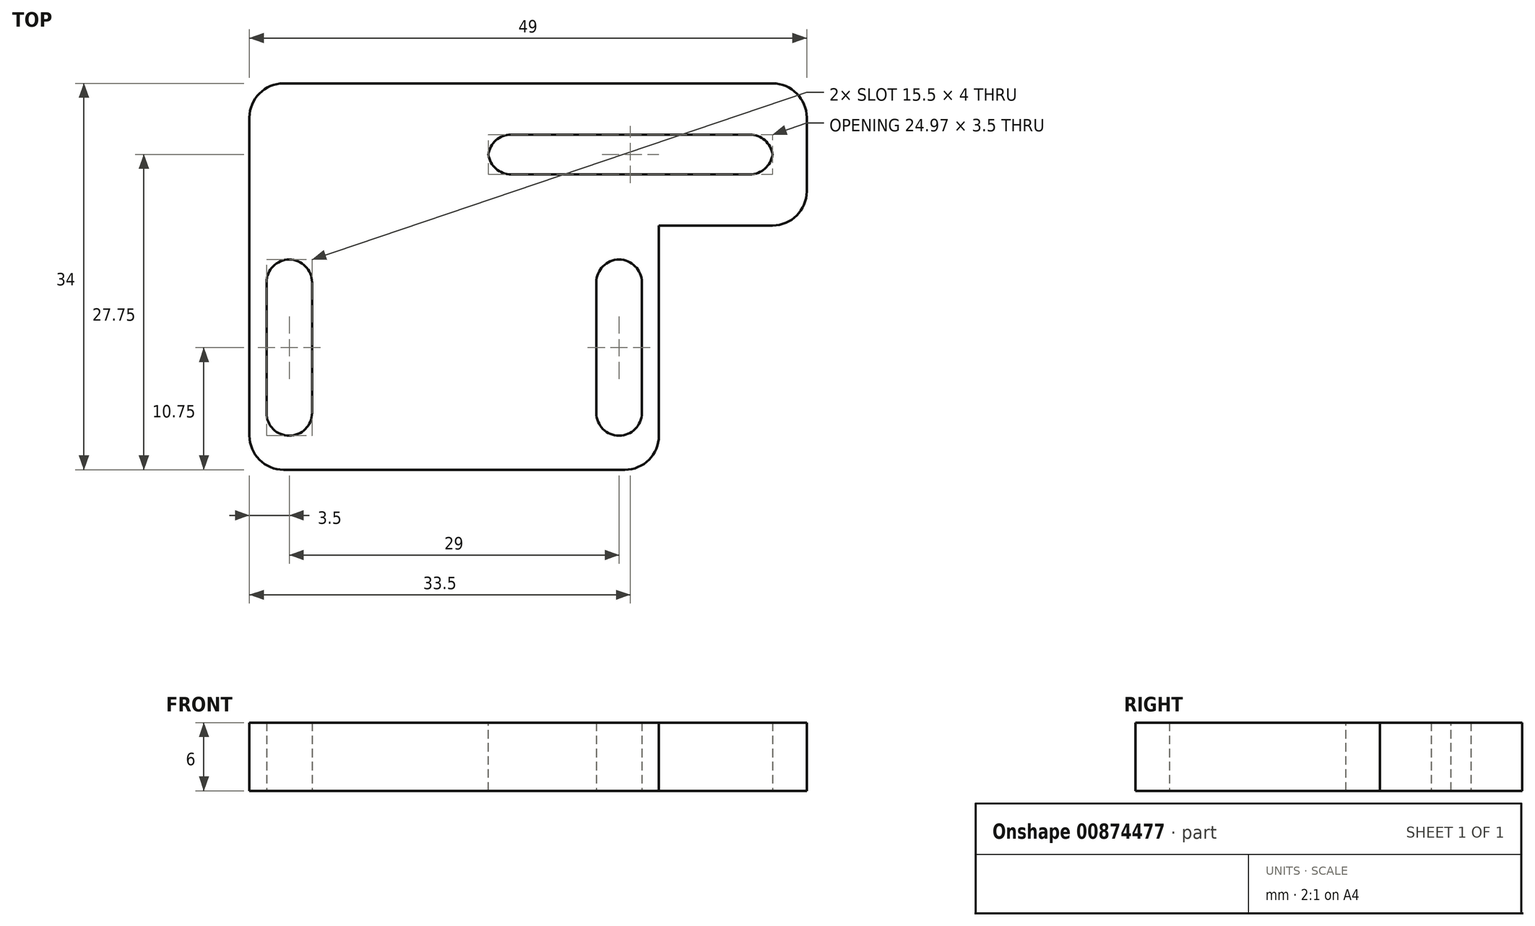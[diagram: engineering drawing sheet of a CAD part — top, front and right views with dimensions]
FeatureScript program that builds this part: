
annotation { "Feature Type Name" : "Feature", "Feature Type Description" : "" }
export const myFeature = defineFeature(function(context is Context, id is Id, definition is map)
    precondition{}
    {
        {
            var Q0;
            Q0=qCreatedBy(makeId("Top.planeOp"),FACE);
            var sketch = newSketch(context, id + "F0", { "sketchPlane" : qUnion([Q0])});
            skLineSegment(sketch, "E0.bottom", {"start": v(18, 10.75) * mm, "end": v(-18, 10.75) * mm});
            skLineSegment(sketch, "E0.top", {"start": v(18, -10.75) * mm, "end": v(-18, -10.75) * mm});
            skLineSegment(sketch, "E0.left", {"start": v(18, 10.75) * mm, "end": v(18, -10.75) * mm});
            skLineSegment(sketch, "E0.right", {"start": v(-18, 10.75) * mm, "end": v(-18, -10.75) * mm});
            skPoint(sketch, "E0.middle", {"position": v(0, 0) * mm});
            skLineSegment(sketch, "E1.bottom", {"start": v(12.5, -7.75) * mm, "end": v(16.5, -7.75) * mm});
            skLineSegment(sketch, "E1.top", {"start": v(12.5, 7.75) * mm, "end": v(16.5, 7.75) * mm});
            skLineSegment(sketch, "E1.left", {"start": v(12.5, -7.75) * mm, "end": v(12.5, 7.75) * mm});
            skLineSegment(sketch, "E1.right", {"start": v(16.5, -7.75) * mm, "end": v(16.5, 7.75) * mm});
            skPoint(sketch, "E1.middle", {"position": v(14.5, 0) * mm});
            skLineSegment(sketch, "E2.bottom", {"start": v(-12.5, 7.75) * mm, "end": v(-16.5, 7.75) * mm});
            skLineSegment(sketch, "E2.top", {"start": v(-12.5, -7.75) * mm, "end": v(-16.5, -7.75) * mm});
            skLineSegment(sketch, "E2.left", {"start": v(-12.5, 7.75) * mm, "end": v(-12.5, -7.75) * mm});
            skLineSegment(sketch, "E2.right", {"start": v(-16.5, 7.75) * mm, "end": v(-16.5, -7.75) * mm});
            skPoint(sketch, "E2.middle", {"position": v(-14.5, 0) * mm});
            skCircle(sketch, "E3", {"center": v(-4.03, -6.69) * mm, "radius": 1.63 * mm});
            skCircle(sketch, "E4", {"center": v(4.03, -6.69) * mm, "radius": 1.63 * mm});
            skLineSegment(sketch, "E5", {"start": v(-4.03, -6.69) * mm, "end": v(4.03, -6.69) * mm, "construction": true});
            skLineSegment(sketch, "E6", {"start": v(0, -6.69) * mm, "end": v(0, 0) * mm, "construction": true});
            skLineSegment(sketch, "E7.bottom", {"start": v(-18, 10.75) * mm, "end": v(31, 10.75) * mm});
            skLineSegment(sketch, "E7.top", {"start": v(-18, 23.25) * mm, "end": v(31, 23.25) * mm});
            skLineSegment(sketch, "E7.left", {"start": v(-18, 10.75) * mm, "end": v(-18, 23.25) * mm});
            skLineSegment(sketch, "E7.right", {"start": v(31, 10.75) * mm, "end": v(31, 23.25) * mm});
            skLineSegment(sketch, "E8.bottom", {"start": v(28, 18.75) * mm, "end": v(3, 18.75) * mm});
            skLineSegment(sketch, "E8.top", {"start": v(28, 15.25) * mm, "end": v(3, 15.25) * mm});
            skLineSegment(sketch, "E8.left", {"start": v(28, 18.75) * mm, "end": v(28, 15.25) * mm});
            skLineSegment(sketch, "E8.right", {"start": v(3, 18.75) * mm, "end": v(3, 15.25) * mm});
            skLineSegment(sketch, "E9", {"start": v(0, 10.75) * mm, "end": v(0, 23.25) * mm, "construction": true});
            skLineSegment(sketch, "E10", {"start": v(28, 17) * mm, "end": v(31, 17) * mm, "construction": true});
            skSolve(sketch);
        }
        {
            var Q0;
            Q0=makeQuery(id+"F0.imprint","IMPRINT",FACE,{"disambiguationData":[TD([[makeQuery(id+"F0.imprint","IMPRINT",EDGE,{"derivedFrom":sQuery(id+"F0.wireOp",EDGE,"E0.top")}),-1.0]])]});
            var Q1;
            Q1=makeQuery(id+"F0.imprint","IMPRINT",FACE,{"disambiguationData":[TD([[makeQuery(id+"F0.imprint","IMPRINT",EDGE,{"derivedFrom":sQuery(id+"F0.wireOp",EDGE,"E7.top")}),-1.0]])]});
            var Q2;
            Q2=makeQuery(id+"F0.imprint","IMPRINT",FACE,{"disambiguationData":[TD([[makeQuery(id+"F0.imprint","IMPRINT",EDGE,{"derivedFrom":sQuery(id+"F0.wireOp",EDGE,"E3")}),1.0]])]});
            var Q3;
            Q3=makeQuery(id+"F0.imprint","IMPRINT",FACE,{"disambiguationData":[TD([[makeQuery(id+"F0.imprint","IMPRINT",EDGE,{"derivedFrom":sQuery(id+"F0.wireOp",EDGE,"E4")}),1.0]])]});
            extrude(context, id + "F1", {"entities" : qUnion([Q0, Q1, Q2, Q3]), "depth" : 6 * mm, "offsetDistance" : 25 * mm});
        }
        {
            var Q0;
            Q0=makeQuery(id+"F1.opExtrude","SWEPT_EDGE",EDGE,{"disambiguationData":[OSD([sQuery(id+"F0.wireOp",EDGE,"E8.bottom"),sQuery(id+"F0.wireOp",EDGE,"E8.right")])]});
            var Q1;
            Q1=makeQuery(id+"F1.opExtrude","SWEPT_EDGE",EDGE,{"disambiguationData":[OSD([sQuery(id+"F0.wireOp",EDGE,"E8.bottom"),sQuery(id+"F0.wireOp",EDGE,"E8.left")])]});
            var Q2;
            Q2=makeQuery(id+"F1.opExtrude","SWEPT_EDGE",EDGE,{"disambiguationData":[OSD([sQuery(id+"F0.wireOp",EDGE,"E8.top"),sQuery(id+"F0.wireOp",EDGE,"E8.left")])]});
            var Q3;
            Q3=makeQuery(id+"F1.opExtrude","SWEPT_EDGE",EDGE,{"disambiguationData":[OSD([sQuery(id+"F0.wireOp",EDGE,"E8.top"),sQuery(id+"F0.wireOp",EDGE,"E8.right")])]});
            var Q4;
            Q4=makeQuery(id+"F1.opExtrude","SWEPT_EDGE",EDGE,{"disambiguationData":[OSD([sQuery(id+"F0.wireOp",EDGE,"E2.top"),sQuery(id+"F0.wireOp",EDGE,"E2.right")])]});
            var Q5;
            Q5=makeQuery(id+"F1.opExtrude","SWEPT_EDGE",EDGE,{"disambiguationData":[OSD([sQuery(id+"F0.wireOp",EDGE,"E1.bottom"),sQuery(id+"F0.wireOp",EDGE,"E1.left")])]});
            var Q6;
            Q6=makeQuery(id+"F1.opExtrude","SWEPT_EDGE",EDGE,{"disambiguationData":[OSD([sQuery(id+"F0.wireOp",EDGE,"E1.bottom"),sQuery(id+"F0.wireOp",EDGE,"E1.right")])]});
            var Q7;
            Q7=makeQuery(id+"F1.opExtrude","SWEPT_EDGE",EDGE,{"disambiguationData":[OSD([sQuery(id+"F0.wireOp",EDGE,"E2.top"),sQuery(id+"F0.wireOp",EDGE,"E2.left")])]});
            var Q8;
            Q8=makeQuery(id+"F1.opExtrude","SWEPT_EDGE",EDGE,{"disambiguationData":[OSD([sQuery(id+"F0.wireOp",EDGE,"E2.bottom"),sQuery(id+"F0.wireOp",EDGE,"E2.left")])]});
            var Q9;
            Q9=makeQuery(id+"F1.opExtrude","SWEPT_EDGE",EDGE,{"disambiguationData":[OSD([sQuery(id+"F0.wireOp",EDGE,"E2.bottom"),sQuery(id+"F0.wireOp",EDGE,"E2.right")])]});
            var Q10;
            Q10=makeQuery(id+"F1.opExtrude","SWEPT_EDGE",EDGE,{"disambiguationData":[OSD([sQuery(id+"F0.wireOp",EDGE,"E1.top"),sQuery(id+"F0.wireOp",EDGE,"E1.left")])]});
            var Q11;
            Q11=makeQuery(id+"F1.opExtrude","SWEPT_EDGE",EDGE,{"disambiguationData":[OSD([sQuery(id+"F0.wireOp",EDGE,"E1.top"),sQuery(id+"F0.wireOp",EDGE,"E1.right")])]});
            fillet(context, id + "F2", {"entities" : qUnion([Q0, Q1, Q2, Q3, Q4, Q5, Q6, Q7, Q8, Q9, Q10, Q11]), "radius" : 2 * mm, "tangentPropagation" : true, "allowEdgeOverflow" : false});
        }
        {
            var Q0;
            Q0=makeQuery(id+"F1.opExtrude","SWEPT_EDGE",EDGE,{"disambiguationData":[OSD([sQuery(id+"F0.wireOp",EDGE,"E7.bottom"),sQuery(id+"F0.wireOp",EDGE,"E7.right")])]});
            var Q1;
            Q1=makeQuery(id+"F1.opExtrude","SWEPT_EDGE",EDGE,{"disambiguationData":[OSD([sQuery(id+"F0.wireOp",EDGE,"E7.top"),sQuery(id+"F0.wireOp",EDGE,"E7.right")])]});
            var Q2;
            Q2=makeQuery(id+"F1.opExtrude","SWEPT_EDGE",EDGE,{"disambiguationData":[OSD([sQuery(id+"F0.wireOp",EDGE,"E7.top"),sQuery(id+"F0.wireOp",EDGE,"E7.left")])]});
            var Q3;
            Q3=makeQuery(id+"F1.opExtrude","SWEPT_EDGE",EDGE,{"disambiguationData":[OSD([sQuery(id+"F0.wireOp",EDGE,"E0.top"),sQuery(id+"F0.wireOp",EDGE,"E0.right")])]});
            var Q4;
            Q4=makeQuery(id+"F1.opExtrude","SWEPT_EDGE",EDGE,{"disambiguationData":[OSD([sQuery(id+"F0.wireOp",EDGE,"E0.top"),sQuery(id+"F0.wireOp",EDGE,"E0.left")])]});
            fillet(context, id + "F3", {"entities" : qUnion([Q0, Q1, Q2, Q3, Q4]), "radius" : 3 * mm, "tangentPropagation" : true, "allowEdgeOverflow" : false});
        }
    });
